# Revit family: Toilet_Seat-Elongated_Closed_Front-Cleansing-KOHLER-C3_255-K-22771K_1
name_source: partatom
category: Plumbing Fixtures
units: mm (PartAtom-declared; Revit-internal decimal feet)

## family parameters
Cut with Voids When Loaded = No
Host = Face
OmniClass Number = 23.31.19.19.17
OmniClass Title = Water Closet Seats
Part Type = Normal
Room Calculation Point = No
Round Connector Dimension = Use Diameter
Shared = No

## types (2) — shared parameters
ADA Compliant = No
Apparent Load = 2200 VA
Assembly Code = D2010100
CW Connection = Yes
Cold Water Inlet = Cold Water Inlet
Date Modified = 10/04/2022
Default Elevation = 15"
Electrical Connector = Yes
Electrical Note = One Dedicated Circuit Required
Finish = Kohler-Plastic-0-White
Flow Rate = 0 GPM
Flush Rate- GPF = 0 GPF
Flush Rate- LPF = 0 LPF
HW Connection = No
Height = 5 1/8"
Hot Water Inlet = Hot Water Inlet
Length = 20 5/8"
Manufacturer = Kohler Co.
Master Format 2014 = 22 41 13.13
Master Format 2014 Name = Residential Water Closets
Material = Plastic
Pressure = 107.33 psi
Product Name = C3-255
URL = https://www.kohlerasiapacific.com
Vent Connection = No
Voltage = 220 V
Waste Connection = No
Waste Water Outlet = Waste Water Outlet
WaterSense Certified = No
Width = 15 1/2"

## per-type parameters (varying)
| type | Description | Model | Type |
| 0-White | TW Version | K-22771K-0 | 1 |
| Hidden Cord, 0-White | TW Version (Hidden Cord) | K-22771K-HC-0 | 2 |

## geometry (parser evidence)
native form markers: Sweep x6
no freeform markers — native parametric forms only
